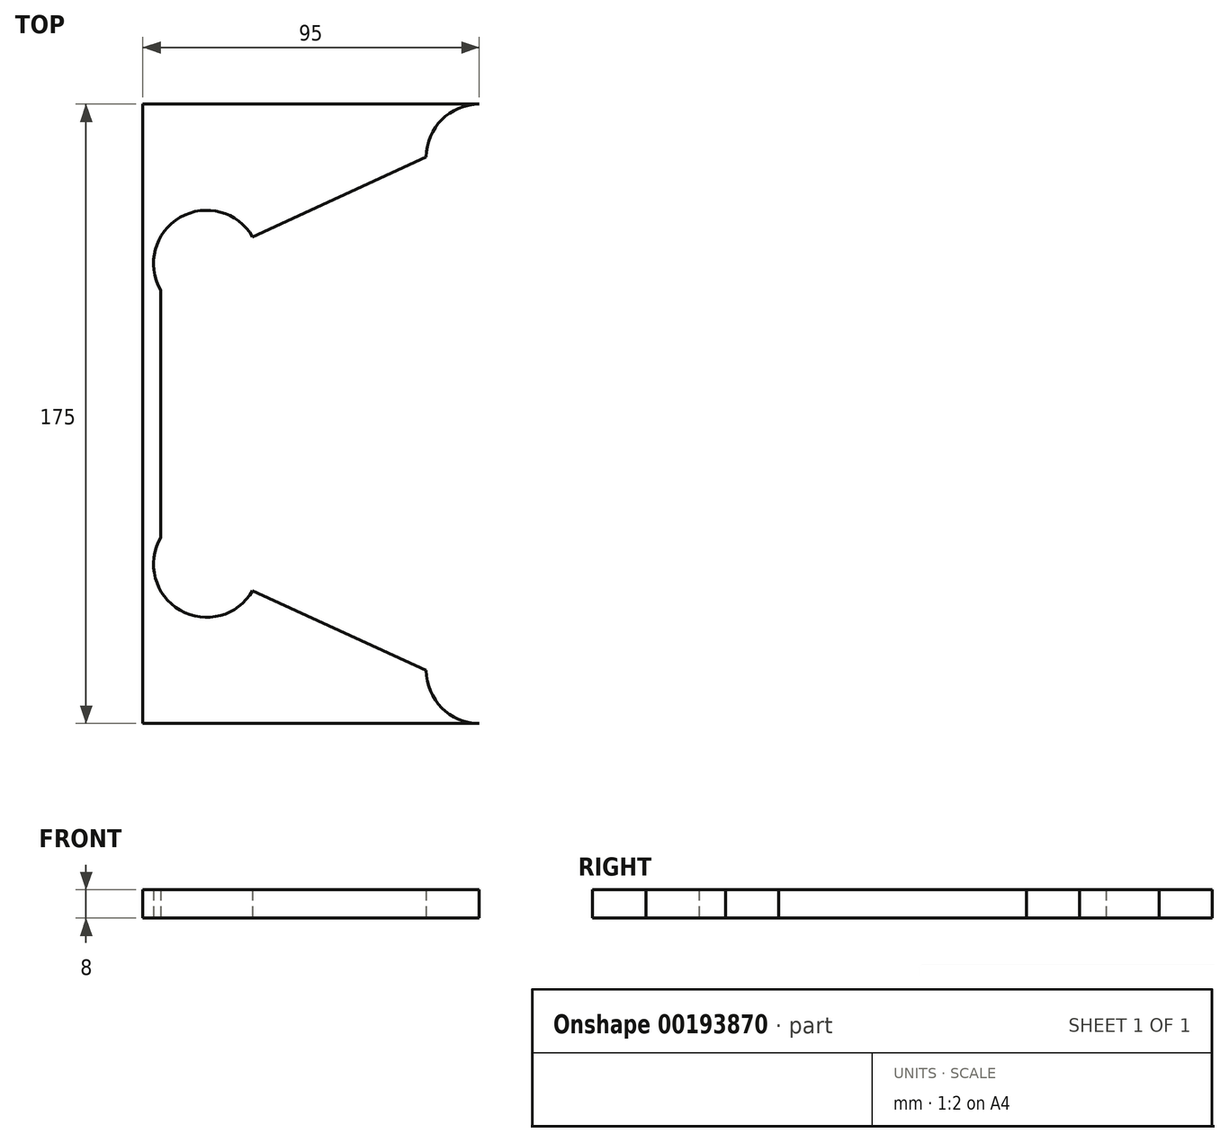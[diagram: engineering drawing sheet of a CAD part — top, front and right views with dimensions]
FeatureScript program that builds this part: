
annotation { "Feature Type Name" : "Feature", "Feature Type Description" : "" }
export const myFeature = defineFeature(function(context is Context, id is Id, definition is map)
    precondition{}
    {
        {
            var Q0;
            Q0=qCreatedBy(makeId("Top.planeOp"),FACE);
            var sketch = newSketch(context, id + "F0", { "sketchPlane" : qUnion([Q0])});
            skLineSegment(sketch, "E0.bottom", {"start": v(95, 87.5) * mm, "end": v(-95, 87.5) * mm});
            skLineSegment(sketch, "E0.top", {"start": v(95, -87.5) * mm, "end": v(-95, -87.5) * mm});
            skLineSegment(sketch, "E0.left", {"start": v(95, 87.5) * mm, "end": v(95, -87.5) * mm});
            skLineSegment(sketch, "E0.right", {"start": v(-95, 87.5) * mm, "end": v(-95, -87.5) * mm});
            skPoint(sketch, "E0.middle", {"position": v(0, 0) * mm});
            skLineSegment(sketch, "E1", {"start": v(-95, 0) * mm, "end": v(95, 0) * mm, "construction": true});
            skSolve(sketch);
        }
        {
            var Q0;
            Q0 = qSketchRegion(id + "F0", true);
            extrude(context, id + "F1", {"entities" : qUnion([Q0]), "depth" : 8 * mm});
        }
        {
            var Q0;
            Q0=makeQuery(id+"F1.opExtrude","CAP_FACE",FACE,{"disambiguationData":[OSD([sQuery(id+"F0.wireOp",EDGE,"E0.bottom"),sQuery(id+"F0.wireOp",EDGE,"E0.top"),sQuery(id+"F0.wireOp",EDGE,"E0.left"),sQuery(id+"F0.wireOp",EDGE,"E0.right")])],"isStart":false});
            var sketch = newSketch(context, id + "F2", { "sketchPlane" : qUnion([Q0])});
            skCircle(sketch, "E2", {"center": v(0, 72.5) * mm, "radius": 4.5 * mm});
            skCircle(sketch, "E3", {"center": v(-77, 42.5) * mm, "radius": 4.5 * mm});
            skCircle(sketch, "E4", {"center": v(8.5, 72.5) * mm, "radius": 1.6 * mm});
            skCircle(sketch, "E5", {"center": v(-8.5, 72.5) * mm, "radius": 1.6 * mm});
            skLineSegment(sketch, "E6", {"start": v(-11.23, 72.5) * mm, "end": v(11.75, 72.5) * mm, "construction": true});
            skLineSegment(sketch, "E7", {"start": v(-92.4, 33.6) * mm, "end": v(-57.68, 53.66) * mm, "construction": true});
            skCircle(sketch, "E8", {"center": v(-84.36, 38.25) * mm, "radius": 1.6 * mm});
            skCircle(sketch, "E9", {"center": v(-69.64, 46.75) * mm, "radius": 1.6 * mm});
            skCircle(sketch, "E10.MirrorC", {"center": v(77, 42.5) * mm, "radius": 4.5 * mm});
            skCircle(sketch, "E11.MirrorC", {"center": v(84.36, 38.25) * mm, "radius": 1.6 * mm});
            skCircle(sketch, "E12.MirrorC", {"center": v(69.64, 46.75) * mm, "radius": 1.6 * mm});
            skCircle(sketch, "E13.MirrorC", {"center": v(-84.36, -38.25) * mm, "radius": 1.6 * mm});
            skCircle(sketch, "E14.MirrorC", {"center": v(-77, -42.5) * mm, "radius": 4.5 * mm});
            skCircle(sketch, "E15.MirrorC", {"center": v(-69.64, -46.75) * mm, "radius": 1.6 * mm});
            skCircle(sketch, "E16.MirrorC", {"center": v(-8.5, -72.5) * mm, "radius": 1.6 * mm});
            skCircle(sketch, "E17.MirrorC", {"center": v(0, -72.5) * mm, "radius": 4.5 * mm});
            skCircle(sketch, "E18.MirrorC", {"center": v(8.5, -72.5) * mm, "radius": 1.6 * mm});
            skCircle(sketch, "E19.MirrorC", {"center": v(69.64, -46.75) * mm, "radius": 1.6 * mm});
            skCircle(sketch, "E20.MirrorC", {"center": v(77, -42.5) * mm, "radius": 4.5 * mm});
            skCircle(sketch, "E21.MirrorC", {"center": v(84.36, -38.25) * mm, "radius": 1.6 * mm});
            skSolve(sketch);
        }
        {
            var Q0;
            Q0 = qSketchRegion(id + "F2", true);
            extrude(context, id + "F3", {"entities" : qUnion([Q0]), "operationType" : NewBodyOperationType.REMOVE, "oppositeDirection" : true, "depth" : 8 * mm});
        }
        {
            var Q0;
            Q0=makeQuery(id+"F1.opExtrude","CAP_FACE",FACE,{"disambiguationData":[OSD([sQuery(id+"F0.wireOp",EDGE,"E0.bottom"),sQuery(id+"F0.wireOp",EDGE,"E0.top"),sQuery(id+"F0.wireOp",EDGE,"E0.left"),sQuery(id+"F0.wireOp",EDGE,"E0.right")])],"isStart":false});
            var sketch = newSketch(context, id + "F4", { "sketchPlane" : qUnion([Q0])});
            skCircle(sketch, "E22.0", {"center": v(0, 72.5) * mm, "radius": 4.5 * mm});
            skArc(sketch, "E23", {"start": v(-15, 72.5) * mm, "mid": v(0, 87.5) * mm, "end": v(15, 72.5) * mm});
            skCircle(sketch, "E24.0", {"center": v(-69.64, 46.75) * mm, "radius": 1.6 * mm});
            skCircle(sketch, "E25.0", {"center": v(-77, 42.5) * mm, "radius": 4.5 * mm});
            skCircle(sketch, "E26.0", {"center": v(-84.36, 38.25) * mm, "radius": 1.6 * mm});
            skLineSegment(sketch, "E27", {"start": v(-77, 42.5) * mm, "end": v(-60.48, 52.04) * mm, "construction": true});
            skLineSegment(sketch, "E28", {"start": v(-77, 42.5) * mm, "end": v(-92.09, 33.8) * mm, "construction": true});
            skArc(sketch, "E29", {"start": v(-90, 35) * mm, "mid": v(-84.5, 55.5) * mm, "end": v(-64, 50) * mm});
            skArc(sketch, "E30.MirrorCS", {"start": v(90, 35) * mm, "mid": v(84.5, 55.5) * mm, "end": v(64, 50) * mm});
            skArc(sketch, "E31.MirrorCS", {"start": v(-90, -35) * mm, "mid": v(-84.5, -55.5) * mm, "end": v(-64, -50) * mm});
            skArc(sketch, "E32.MirrorCS", {"start": v(-15, -72.5) * mm, "mid": v(0, -87.5) * mm, "end": v(15, -72.5) * mm});
            skArc(sketch, "E33.MirrorCS", {"start": v(90, -35) * mm, "mid": v(84.5, -55.5) * mm, "end": v(64, -50) * mm});
            skLineSegment(sketch, "E34", {"start": v(-64, 50) * mm, "end": v(-15, 72.5) * mm});
            skLineSegment(sketch, "E35", {"start": v(15, 72.5) * mm, "end": v(64, 50) * mm});
            skLineSegment(sketch, "E36", {"start": v(90, 35) * mm, "end": v(90, -35) * mm});
            skLineSegment(sketch, "E37", {"start": v(64, -50) * mm, "end": v(15, -72.5) * mm});
            skLineSegment(sketch, "E38", {"start": v(-15, -72.5) * mm, "end": v(-64, -50) * mm});
            skLineSegment(sketch, "E39", {"start": v(-90, -35) * mm, "end": v(-90, 35) * mm});
            skLineSegment(sketch, "E40.0", {"start": v(95, 87.5) * mm, "end": v(-95, 87.5) * mm});
            skLineSegment(sketch, "E41.0", {"start": v(-95, 87.5) * mm, "end": v(-95, -87.5) * mm});
            skLineSegment(sketch, "E42.0", {"start": v(95, 87.5) * mm, "end": v(95, -87.5) * mm});
            skLineSegment(sketch, "E43.0", {"start": v(95, -87.5) * mm, "end": v(-95, -87.5) * mm});
            skLineSegment(sketch, "E44", {"start": v(-95, 87.5) * mm, "end": v(95, 87.5) * mm});
            skLineSegment(sketch, "E45", {"start": v(-95, -87.5) * mm, "end": v(-95, 87.5) * mm});
            skSolve(sketch);
        }
        {
            var Q0;
            Q0=makeQuery(id+"F4.imprint","IMPRINT",FACE,{"disambiguationData":[TD([[makeQuery(id+"F4.imprint","IMPRINT",EDGE,{"derivedFrom":sQuery(id+"F4.wireOp",EDGE,"E29")}),1.0]])]});
            var Q1;
            Q1=makeQuery(id+"F4.imprint","IMPRINT",FACE,{"disambiguationData":[TD([[makeQuery(id+"F4.imprint","IMPRINT",EDGE,{"derivedFrom":sQuery(id+"F4.wireOp",EDGE,"E30.MirrorCS")}),-1.0]])]});
            extrude(context, id + "F5", {"entities" : qUnion([Q0, Q1]), "operationType" : NewBodyOperationType.REMOVE, "endBound" : BoundingType.THROUGH_ALL, "oppositeDirection" : true, "depth" : 25 * mm});
        }
        {
            var Q0;
            Q0=makeQuery(id+"F1.opExtrude","CAP_FACE",FACE,{"disambiguationData":[OSD([sQuery(id+"F0.wireOp",EDGE,"E0.bottom"),sQuery(id+"F0.wireOp",EDGE,"E0.top"),sQuery(id+"F0.wireOp",EDGE,"E0.left"),sQuery(id+"F0.wireOp",EDGE,"E0.right")])],"isStart":false});
            var sketch = newSketch(context, id + "F6", { "sketchPlane" : qUnion([Q0])});
            skCircle(sketch, "E46.0", {"center": v(-77, 42.5) * mm, "radius": 4.5 * mm});
            skCircle(sketch, "E47.0", {"center": v(0, 72.5) * mm, "radius": 4.5 * mm});
            skCircle(sketch, "E48", {"center": v(0, 72.5) * mm, "radius": 12.2 * mm});
            skCircle(sketch, "E49", {"center": v(-77, 42.5) * mm, "radius": 12.2 * mm});
            skCircle(sketch, "E50.MirrorC", {"center": v(77, 42.5) * mm, "radius": 12.2 * mm});
            skCircle(sketch, "E51.MirrorC", {"center": v(-77, -42.5) * mm, "radius": 12.2 * mm});
            skCircle(sketch, "E52.MirrorC", {"center": v(0, -72.5) * mm, "radius": 12.2 * mm});
            skCircle(sketch, "E53.MirrorC", {"center": v(77, -42.5) * mm, "radius": 12.2 * mm});
            skSolve(sketch);
        }
        {
            var Q0;
            Q0 = qSketchRegion(id + "F6", true);
            extrude(context, id + "F7", {"entities" : qUnion([Q0]), "operationType" : NewBodyOperationType.REMOVE, "oppositeDirection" : true, "depth" : 4 * mm});
        }
        {
            var Q0;
            Q0=makeQuery(id+"F1.opExtrude","CAP_FACE",FACE,{"disambiguationData":[OSD([sQuery(id+"F0.wireOp",EDGE,"E0.bottom"),sQuery(id+"F0.wireOp",EDGE,"E0.top"),sQuery(id+"F0.wireOp",EDGE,"E0.left"),sQuery(id+"F0.wireOp",EDGE,"E0.right")])],"isStart":false});
            var sketch = newSketch(context, id + "F8", { "sketchPlane" : qUnion([Q0])});
            skCircle(sketch, "E54", {"center": v(0, 45) * mm, "radius": 1.7 * mm});
            skCircle(sketch, "E55", {"center": v(0, 26.6) * mm, "radius": 1.7 * mm});
            skCircle(sketch, "E56", {"center": v(-67.5, 26.6) * mm, "radius": 1.7 * mm});
            skCircle(sketch, "E57", {"center": v(-35, 26.6) * mm, "radius": 1.7 * mm});
            skCircle(sketch, "E58", {"center": v(35, 26.6) * mm, "radius": 1.7 * mm});
            skCircle(sketch, "E59", {"center": v(67.5, 26.6) * mm, "radius": 1.7 * mm});
            skLineSegment(sketch, "E60", {"start": v(-67.5, 26.6) * mm, "end": v(67.5, 26.6) * mm, "construction": true});
            skCircle(sketch, "E61.MirrorC", {"center": v(67.5, -26.6) * mm, "radius": 1.7 * mm});
            skCircle(sketch, "E62.MirrorC", {"center": v(35, -26.6) * mm, "radius": 1.7 * mm});
            skCircle(sketch, "E63.MirrorC", {"center": v(0, -26.6) * mm, "radius": 1.7 * mm});
            skCircle(sketch, "E64.MirrorC", {"center": v(0, -45) * mm, "radius": 1.7 * mm});
            skCircle(sketch, "E65.MirrorC", {"center": v(-35, -26.6) * mm, "radius": 1.7 * mm});
            skCircle(sketch, "E66.MirrorC", {"center": v(-67.5, -26.6) * mm, "radius": 1.7 * mm});
            skLineSegment(sketch, "E67.bottom", {"start": v(72.5, -16.6) * mm, "end": v(-72.5, -16.6) * mm});
            skLineSegment(sketch, "E67.top", {"start": v(72.5, 16.6) * mm, "end": v(-72.5, 16.6) * mm});
            skLineSegment(sketch, "E67.left", {"start": v(72.5, -16.6) * mm, "end": v(72.5, 16.6) * mm});
            skLineSegment(sketch, "E67.right", {"start": v(-72.5, -16.6) * mm, "end": v(-72.5, 16.6) * mm});
            skPoint(sketch, "E67.middle", {"position": v(0, 0) * mm});
            skCircle(sketch, "E68", {"center": v(-80, 0) * mm, "radius": 1.8 * mm});
            skSolve(sketch);
        }
        {
            var Q0;
            Q0 = qSketchRegion(id + "F8", true);
            extrude(context, id + "F9", {"entities" : qUnion([Q0]), "operationType" : NewBodyOperationType.REMOVE, "endBound" : BoundingType.THROUGH_ALL, "oppositeDirection" : true, "depth" : 25 * mm});
        }
        {
            var Q0;
            Q0=makeQuery(id+"F1.opExtrude","SWEPT_BODY",BODY,{"disambiguationData":[OSD([sQuery(id+"F0.wireOp",EDGE,"E0.bottom"),sQuery(id+"F0.wireOp",EDGE,"E0.top"),sQuery(id+"F0.wireOp",EDGE,"E0.left"),sQuery(id+"F0.wireOp",EDGE,"E0.right")])]});
            var Q1;
            Q1=sQuery(id+"F0.wireOp",EDGE,"E1");
            transform(context, id + "F10", {"entities" : qUnion([Q0]), "transformType" : TransformType.ROTATION, "transformAxis" : qUnion([Q1]), "angle" : 180 * degree, "makeCopy" : false});
        }
        {
            var Q0;
            Q0=makeQuery(id+"F1.opExtrude","SWEPT_BODY",BODY,{"disambiguationData":[OSD([sQuery(id+"F0.wireOp",EDGE,"E0.bottom"),sQuery(id+"F0.wireOp",EDGE,"E0.top"),sQuery(id+"F0.wireOp",EDGE,"E0.left"),sQuery(id+"F0.wireOp",EDGE,"E0.right")])]});
            transform(context, id + "F11", {"entities" : qUnion([Q0]), "transformType" : TransformType.TRANSLATION_3D, "dx" : 0 * mm, "dy" : 0 * mm, "dz" : 56.2 * mm, "makeCopy" : false});
        }
        {
            var Q0;
            Q0=makeQuery(id+"F1.opExtrude","SWEPT_BODY",BODY,{"disambiguationData":[OSD([sQuery(id+"F0.wireOp",EDGE,"E0.bottom"),sQuery(id+"F0.wireOp",EDGE,"E0.top"),sQuery(id+"F0.wireOp",EDGE,"E0.left"),sQuery(id+"F0.wireOp",EDGE,"E0.right")])]});
            transform(context, id + "F12", {"entities" : qUnion([Q0]), "transformType" : TransformType.TRANSLATION_3D, "dx" : 0 * mm, "dy" : 0 * mm, "dz" : 4.8 * mm, "makeCopy" : false});
        }
        {
            var Q0;
            Q0=makeQuery(id+"F1.opExtrude","CAP_FACE",FACE,{"disambiguationData":[OSD([sQuery(id+"F0.wireOp",EDGE,"E0.bottom"),sQuery(id+"F0.wireOp",EDGE,"E0.top"),sQuery(id+"F0.wireOp",EDGE,"E0.left"),sQuery(id+"F0.wireOp",EDGE,"E0.right")])],"isStart":true});
            var sketch = newSketch(context, id + "F13", { "sketchPlane" : qUnion([Q0])});
            skCircle(sketch, "E69", {"center": v(-80, 0) * mm, "radius": 1.8 * mm});
            skSolve(sketch);
        }
    });
